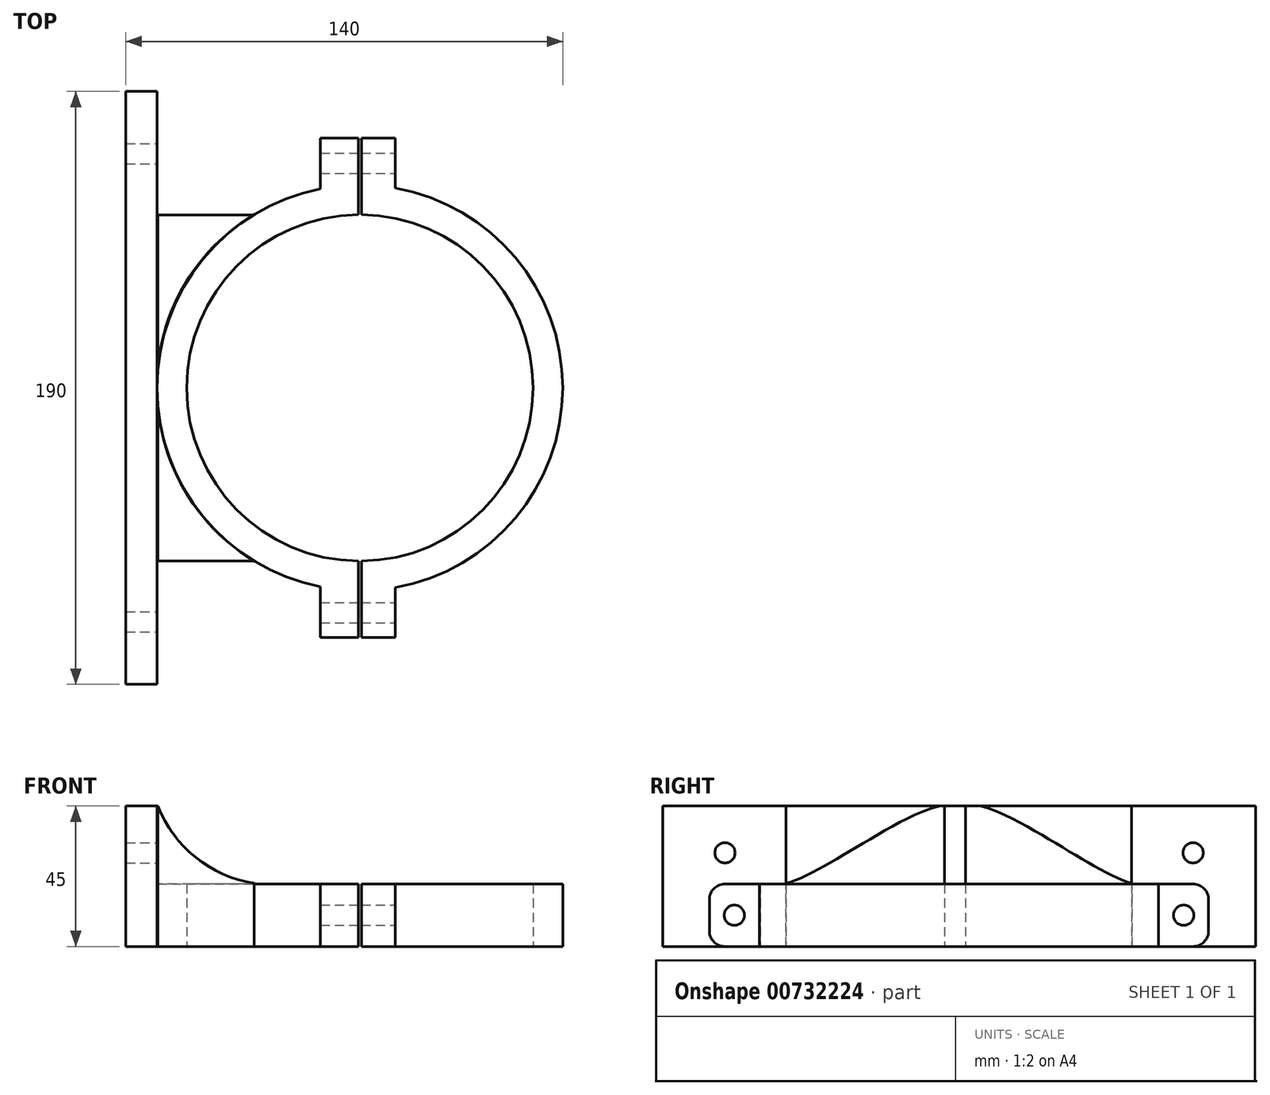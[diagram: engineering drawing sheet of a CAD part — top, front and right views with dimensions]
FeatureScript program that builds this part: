
annotation { "Feature Type Name" : "Feature", "Feature Type Description" : "" }
export const myFeature = defineFeature(function(context is Context, id is Id, definition is map)
    precondition{}
    {
        {
            var Q0;
            Q0=qCreatedBy(makeId("Top.planeOp"),FACE);
            var sketch = newSketch(context, id + "F0", { "sketchPlane" : qUnion([Q0])});
            skCircle(sketch, "E0", {"center": v(0, 0) * mm, "radius": 55.5 * mm});
            skCircle(sketch, "E1", {"center": v(0, 0) * mm, "radius": 65 * mm});
            skLineSegment(sketch, "E2.bottom", {"start": v(-75, 95) * mm, "end": v(-65, 95) * mm});
            skLineSegment(sketch, "E2.top", {"start": v(-75, -95) * mm, "end": v(-65, -95) * mm});
            skLineSegment(sketch, "E2.left", {"start": v(-75, 95) * mm, "end": v(-75, -95) * mm});
            skLineSegment(sketch, "E2.right", {"start": v(-65, 95) * mm, "end": v(-65, -95) * mm});
            skLineSegment(sketch, "E3.bottom", {"start": v(-12.63, 80) * mm, "end": v(11.37, 80) * mm});
            skLineSegment(sketch, "E3.top", {"start": v(-12.63, -80) * mm, "end": v(11.37, -80) * mm});
            skLineSegment(sketch, "E3.left", {"start": v(-12.63, 80) * mm, "end": v(-12.63, 63.76) * mm});
            skLineSegment(sketch, "E3.right", {"start": v(11.37, 80) * mm, "end": v(11.37, 64) * mm});
            skLineSegment(sketch, "E4.trimOffspring", {"start": v(11.37, -64) * mm, "end": v(11.37, -80) * mm});
            skLineSegment(sketch, "E5.trimOffspring", {"start": v(-12.63, -63.76) * mm, "end": v(-12.63, -80) * mm});
            skSolve(sketch);
        }
        {
            var Q0;
            {var subQ1=sQuery(id+"F0.wireOp",EDGE,"E2.bottom");Q0=makeQuery(id+"F0.imprint","IMPRINT",FACE,{"disambiguationData":[TD([[makeQuery(id+"F0.imprint","IMPRINT",EDGE,{"derivedFrom":subQ1}),-1.0]])]});}
            var Q1;
            Q1=makeQuery(id+"F0.imprint","IMPRINT",FACE,{"disambiguationData":[TD([[makeQuery(id+"F0.imprint","IMPRINT",EDGE,{"derivedFrom":sQuery(id+"F0.wireOp",EDGE,"E0")}),-1.0]])]});
            var Q2;
            Q2=makeQuery(id+"F0.imprint","IMPRINT",FACE,{"disambiguationData":[TD([[makeQuery(id+"F0.imprint","IMPRINT",EDGE,{"derivedFrom":sQuery(id+"F0.wireOp",EDGE,"E3.bottom")}),-1.0]])]});
            var Q3;
            Q3=makeQuery(id+"F0.imprint","IMPRINT",FACE,{"disambiguationData":[TD([[makeQuery(id+"F0.imprint","IMPRINT",EDGE,{"derivedFrom":sQuery(id+"F0.wireOp",EDGE,"E3.top")}),1.0]])]});
            extrude(context, id + "F1", {"entities" : qUnion([Q0, Q1, Q2, Q3]), "depth" : 20 * mm, "offsetDistance" : 25 * mm});
        }
        {
            var Q0;
            Q0=makeQuery(id+"F1.opExtrude","SWEPT_FACE",FACE,{"disambiguationData":[OSD([sQuery(id+"F0.wireOp",EDGE,"E4.trimOffspring")])]});
            var sketch = newSketch(context, id + "F2", { "sketchPlane" : qUnion([Q0])});
            skCircle(sketch, "E6", {"center": v(-72, 10) * mm, "radius": 3.25 * mm});
            skPoint(sketch, "E6.centerSnap0", {"position": v(-80, 10) * mm});
            skCircle(sketch, "E7", {"center": v(72, 10) * mm, "radius": 3.25 * mm});
            skSolve(sketch);
        }
        {
            var Q0;
            Q0=makeQuery(id+"F2.imprint","IMPRINT",FACE,{"disambiguationData":[TD([[makeQuery(id+"F2.imprint","IMPRINT",EDGE,{"derivedFrom":sQuery(id+"F2.wireOp",EDGE,"E6")}),1.0]])]});
            var Q1;
            Q1=makeQuery(id+"F2.imprint","IMPRINT",FACE,{"disambiguationData":[TD([[makeQuery(id+"F2.imprint","IMPRINT",EDGE,{"derivedFrom":sQuery(id+"F2.wireOp",EDGE,"E7")}),1.0]])]});
            extrude(context, id + "F3", {"entities" : qUnion([Q0, Q1]), "operationType" : NewBodyOperationType.REMOVE, "endBound" : BoundingType.UP_TO_NEXT, "oppositeDirection" : true, "depth" : 25 * mm, "offsetDistance" : 25 * mm});
        }
        {
            var Q0;
            Q0=makeQuery(id+"F1.opExtrude","CAP_FACE",FACE,{"disambiguationData":[OSD([sQuery(id+"F0.wireOp",EDGE,"E2.bottom"),sQuery(id+"F0.wireOp",EDGE,"E2.top"),sQuery(id+"F0.wireOp",EDGE,"E2.left"),sQuery(id+"F0.wireOp",EDGE,"E2.right")])],"isStart":false});
            var sketch = newSketch(context, id + "F4", { "sketchPlane" : qUnion([Q0])});
            skLineSegment(sketch, "E8.bottom", {"start": v(-75, 95) * mm, "end": v(-65, 95) * mm});
            skLineSegment(sketch, "E8.top", {"start": v(-75, -95) * mm, "end": v(-65, -95) * mm});
            skLineSegment(sketch, "E8.left", {"start": v(-75, 95) * mm, "end": v(-75, -95) * mm});
            skLineSegment(sketch, "E8.right", {"start": v(-65, 95) * mm, "end": v(-65, -95) * mm});
            skSolve(sketch);
        }
        {
            var Q0;
            Q0=makeQuery(id+"F4.imprint","IMPRINT",FACE,{"disambiguationData":[TD([[makeQuery(id+"F4.imprint","IMPRINT",EDGE,{"derivedFrom":sQuery(id+"F4.wireOp",EDGE,"E8.bottom")}),-1.0]])]});
            extrude(context, id + "F5", {"entities" : qUnion([Q0]), "operationType" : NewBodyOperationType.ADD, "depth" : 25 * mm, "offsetDistance" : 25 * mm});
        }
        {
            var Q0;
            Q0=makeQuery(id+"F1.opExtrude","CAP_FACE",FACE,{"disambiguationData":[OSD([sQuery(id+"F0.wireOp",EDGE,"E0"),sQuery(id+"F0.wireOp",EDGE,"E1"),sQuery(id+"F0.wireOp",EDGE,"E3.bottom"),sQuery(id+"F0.wireOp",EDGE,"E3.top"),sQuery(id+"F0.wireOp",EDGE,"E3.left"),sQuery(id+"F0.wireOp",EDGE,"E3.right"),sQuery(id+"F0.wireOp",EDGE,"E4.trimOffspring"),sQuery(id+"F0.wireOp",EDGE,"E5.trimOffspring")])],"isStart":true});
            var sketch = newSketch(context, id + "F6", { "sketchPlane" : qUnion([Q0])});
            skLineSegment(sketch, "E9", {"start": v(-33.92, 55.45) * mm, "end": v(-64.72, 55.45) * mm});
            skLineSegment(sketch, "E10", {"start": v(-34.05, -55.37) * mm, "end": v(-64.72, -55.37) * mm});
            skArc(sketch, "E11", {"start": v(-33.92, 55.45) * mm, "mid": v(-55.58, 33.8) * mm, "end": v(-64.84, 4.62) * mm});
            skArc(sketch, "E12", {"start": v(-65, 0) * mm, "mid": v(-56.9, -31.8) * mm, "end": v(-34.05, -55.37) * mm});
            skLineSegment(sketch, "E13", {"start": v(-64.72, 55.45) * mm, "end": v(-64.84, 4.62) * mm});
            skLineSegment(sketch, "E14", {"start": v(-65, 0) * mm, "end": v(-64.72, -55.37) * mm});
            skSolve(sketch);
        }
        {
            var Q0;
            Q0=makeQuery(id+"F6.imprint","IMPRINT",FACE,{"disambiguationData":[TD([[makeQuery(id+"F6.imprint","IMPRINT",EDGE,{"derivedFrom":sQuery(id+"F6.wireOp",EDGE,"E9")}),1.0]])]});
            var Q1;
            {var subQ0=sQuery(id+"F6.wireOp",EDGE,"E10");Q1=makeQuery(id+"F6.imprint","IMPRINT",FACE,{"disambiguationData":[TD([[makeQuery(id+"F6.imprint","IMPRINT",EDGE,{"derivedFrom":subQ0}),-1.0]])]});}
            extrude(context, id + "F7", {"entities" : qUnion([Q0, Q1]), "oppositeDirection" : true, "depth" : 45 * mm, "offsetDistance" : 25 * mm});
        }
        {
            var Q0;
            Q0=makeQuery(id+"F7.opExtrude","SWEPT_FACE",FACE,{"disambiguationData":[OSD([sQuery(id+"F6.wireOp",EDGE,"E9")])]});
            var sketch = newSketch(context, id + "F8", { "sketchPlane" : qUnion([Q0])});
            skArc(sketch, "E15", {"start": v(-64.72, 45) * mm, "mid": v(-52.58, 28.55) * mm, "end": v(-33.92, 20.21) * mm});
            skLineSegment(sketch, "E16", {"start": v(-64.72, 45) * mm, "end": v(-33.92, 45) * mm});
            skLineSegment(sketch, "E17", {"start": v(-33.92, 45) * mm, "end": v(-33.92, 20.21) * mm});
            skSolve(sketch);
        }
        {
            var Q0;
            Q0=makeQuery(id+"F8.imprint","IMPRINT",FACE,{"disambiguationData":[TD([[makeQuery(id+"F8.imprint","IMPRINT",EDGE,{"derivedFrom":sQuery(id+"F8.wireOp",EDGE,"E15")}),1.0]])]});
            extrude(context, id + "F9", {"entities" : qUnion([Q0]), "operationType" : NewBodyOperationType.REMOVE, "oppositeDirection" : true, "depth" : 150 * mm, "offsetDistance" : 25 * mm});
        }
        {
            var Q0;
            Q0=makeQuery(id+"F5.boolean.opBoolean","MERGE",FACE,{"derivedFrom":[makeQuery(id+"F1.opExtrude","SWEPT_FACE",FACE,{"disambiguationData":[OSD([sQuery(id+"F0.wireOp",EDGE,"E2.right")])]}),makeQuery(id+"F5.opExtrude","SWEPT_FACE",FACE,{"disambiguationData":[OSD([sQuery(id+"F4.wireOp",EDGE,"E8.right")])]})]});
            var sketch = newSketch(context, id + "F10", { "sketchPlane" : qUnion([Q0])});
            skCircle(sketch, "E18", {"center": v(-75, 30) * mm, "radius": 3.25 * mm});
            skCircle(sketch, "E19", {"center": v(75, 30) * mm, "radius": 3.25 * mm});
            skSolve(sketch);
        }
        {
            var Q0;
            Q0=makeQuery(id+"F10.imprint","IMPRINT",FACE,{"disambiguationData":[TD([[makeQuery(id+"F10.imprint","IMPRINT",EDGE,{"derivedFrom":sQuery(id+"F10.wireOp",EDGE,"E18")}),1.0]])]});
            var Q1;
            Q1=makeQuery(id+"F10.imprint","IMPRINT",FACE,{"disambiguationData":[TD([[makeQuery(id+"F10.imprint","IMPRINT",EDGE,{"derivedFrom":sQuery(id+"F10.wireOp",EDGE,"E19")}),1.0]])]});
            extrude(context, id + "F11", {"entities" : qUnion([Q0, Q1]), "operationType" : NewBodyOperationType.REMOVE, "oppositeDirection" : true, "depth" : 25 * mm, "offsetDistance" : 25 * mm});
        }
        {
            var Q0;
            Q0=makeQuery(id+"F1.opExtrude","CAP_FACE",FACE,{"disambiguationData":[OSD([sQuery(id+"F0.wireOp",EDGE,"E0"),sQuery(id+"F0.wireOp",EDGE,"E1"),sQuery(id+"F0.wireOp",EDGE,"E3.bottom"),sQuery(id+"F0.wireOp",EDGE,"E3.top"),sQuery(id+"F0.wireOp",EDGE,"E3.left"),sQuery(id+"F0.wireOp",EDGE,"E3.right"),sQuery(id+"F0.wireOp",EDGE,"E4.trimOffspring"),sQuery(id+"F0.wireOp",EDGE,"E5.trimOffspring")])],"isStart":false});
            var sketch = newSketch(context, id + "F12", { "sketchPlane" : qUnion([Q0])});
            skLineSegment(sketch, "E20.bottom", {"start": v(-0.5, 86.3) * mm, "end": v(0.5, 86.3) * mm});
            skLineSegment(sketch, "E20.top", {"start": v(-0.5, -88.7) * mm, "end": v(0.5, -88.7) * mm});
            skLineSegment(sketch, "E20.left", {"start": v(-0.5, 86.3) * mm, "end": v(-0.5, -88.7) * mm});
            skLineSegment(sketch, "E20.right", {"start": v(0.5, 86.3) * mm, "end": v(0.5, -88.7) * mm});
            skSolve(sketch);
        }
        {
            var Q0;
            {var subQ0=sQuery(id+"F12.wireOp",EDGE,"E20.left");var subQ1=makeQuery(id+"F1.opExtrude","CAP_EDGE",EDGE,{"disambiguationData":[OSD([sQuery(id+"F0.wireOp",EDGE,"E3.bottom")])],"isStart":false});var subQ2=makeQuery(id+"F12.imprint","INTERSECT",VERTEX,{"derivedFrom":[subQ1,subQ0]});Q0=makeQuery(id+"F12.imprint","IMPRINT",FACE,{"disambiguationData":[TD([[makeQuery(id+"F12.imprint","IMPRINT",EDGE,{"disambiguationData":[TD([[subQ2,-1.0]])],"derivedFrom":subQ0}),1.0]])]});}
            var Q1;
            {var subQ0=sQuery(id+"F12.wireOp",EDGE,"E20.left");var subQ1=makeQuery(id+"F1.opExtrude","CAP_EDGE",EDGE,{"disambiguationData":[OSD([sQuery(id+"F0.wireOp",EDGE,"E3.top")])],"isStart":false});var subQ2=makeQuery(id+"F12.imprint","INTERSECT",VERTEX,{"derivedFrom":[subQ1,subQ0]});Q1=makeQuery(id+"F12.imprint","IMPRINT",FACE,{"disambiguationData":[TD([[makeQuery(id+"F12.imprint","IMPRINT",EDGE,{"disambiguationData":[TD([[subQ2,1.0]])],"derivedFrom":subQ0}),1.0]])]});}
            extrude(context, id + "F13", {"entities" : qUnion([Q0, Q1]), "operationType" : NewBodyOperationType.REMOVE, "oppositeDirection" : true, "depth" : 25 * mm, "offsetDistance" : 25 * mm});
        }
        {
            var Q0;
            {var subQ0=sQuery(id+"F0.wireOp",EDGE,"E5.trimOffspring");var subQ1=sQuery(id+"F0.wireOp",EDGE,"E3.top");Q0=makeQuery(id+"F13.boolean.opBoolean","SPLIT",EDGE,{"disambiguationData":[TD([makeQuery(id+"F1.opExtrude","SWEPT_FACE",FACE,{"disambiguationData":[OSD([subQ0])]})])],"derivedFrom":makeQuery(id+"F1.opExtrude","CAP_EDGE",EDGE,{"disambiguationData":[OSD([subQ1])],"isStart":true})});}
            var Q1;
            {var subQ0=sQuery(id+"F0.wireOp",EDGE,"E4.trimOffspring");var subQ1=sQuery(id+"F0.wireOp",EDGE,"E3.top");Q1=makeQuery(id+"F13.boolean.opBoolean","SPLIT",EDGE,{"disambiguationData":[TD([makeQuery(id+"F1.opExtrude","SWEPT_FACE",FACE,{"disambiguationData":[OSD([subQ0])]})])],"derivedFrom":makeQuery(id+"F1.opExtrude","CAP_EDGE",EDGE,{"disambiguationData":[OSD([subQ1])],"isStart":true})});}
            var Q2;
            {var subQ0=sQuery(id+"F0.wireOp",EDGE,"E4.trimOffspring");var subQ1=sQuery(id+"F0.wireOp",EDGE,"E3.top");var subQ4=makeQuery(id+"F1.opExtrude","CAP_EDGE",EDGE,{"disambiguationData":[OSD([subQ1])],"isStart":false});Q2=makeQuery(id+"F13.boolean.opBoolean","SPLIT",EDGE,{"disambiguationData":[TD([makeQuery(id+"F1.opExtrude","SWEPT_FACE",FACE,{"disambiguationData":[OSD([subQ0])]})])],"derivedFrom":subQ4});}
            var Q3;
            {var subQ0=sQuery(id+"F0.wireOp",EDGE,"E5.trimOffspring");var subQ1=sQuery(id+"F0.wireOp",EDGE,"E3.top");var subQ4=makeQuery(id+"F1.opExtrude","CAP_EDGE",EDGE,{"disambiguationData":[OSD([subQ1])],"isStart":false});Q3=makeQuery(id+"F13.boolean.opBoolean","SPLIT",EDGE,{"disambiguationData":[TD([makeQuery(id+"F1.opExtrude","SWEPT_FACE",FACE,{"disambiguationData":[OSD([subQ0])]})])],"derivedFrom":subQ4});}
            var Q4;
            {var subQ0=sQuery(id+"F0.wireOp",EDGE,"E3.left");var subQ1=sQuery(id+"F0.wireOp",EDGE,"E3.bottom");Q4=makeQuery(id+"F13.boolean.opBoolean","SPLIT",EDGE,{"disambiguationData":[TD([makeQuery(id+"F1.opExtrude","SWEPT_FACE",FACE,{"disambiguationData":[OSD([subQ0])]})])],"derivedFrom":makeQuery(id+"F1.opExtrude","CAP_EDGE",EDGE,{"disambiguationData":[OSD([subQ1])],"isStart":true})});}
            var Q5;
            {var subQ0=sQuery(id+"F0.wireOp",EDGE,"E3.right");var subQ1=sQuery(id+"F0.wireOp",EDGE,"E3.bottom");Q5=makeQuery(id+"F13.boolean.opBoolean","SPLIT",EDGE,{"disambiguationData":[TD([makeQuery(id+"F1.opExtrude","SWEPT_FACE",FACE,{"disambiguationData":[OSD([subQ0])]})])],"derivedFrom":makeQuery(id+"F1.opExtrude","CAP_EDGE",EDGE,{"disambiguationData":[OSD([subQ1])],"isStart":true})});}
            var Q6;
            {var subQ0=sQuery(id+"F0.wireOp",EDGE,"E3.left");var subQ1=sQuery(id+"F0.wireOp",EDGE,"E3.bottom");var subQ4=makeQuery(id+"F1.opExtrude","CAP_EDGE",EDGE,{"disambiguationData":[OSD([subQ1])],"isStart":false});Q6=makeQuery(id+"F13.boolean.opBoolean","SPLIT",EDGE,{"disambiguationData":[TD([makeQuery(id+"F1.opExtrude","SWEPT_FACE",FACE,{"disambiguationData":[OSD([subQ0])]})])],"derivedFrom":subQ4});}
            var Q7;
            {var subQ0=sQuery(id+"F0.wireOp",EDGE,"E3.right");var subQ1=sQuery(id+"F0.wireOp",EDGE,"E3.bottom");var subQ4=makeQuery(id+"F1.opExtrude","CAP_EDGE",EDGE,{"disambiguationData":[OSD([subQ1])],"isStart":false});Q7=makeQuery(id+"F13.boolean.opBoolean","SPLIT",EDGE,{"disambiguationData":[TD([makeQuery(id+"F1.opExtrude","SWEPT_FACE",FACE,{"disambiguationData":[OSD([subQ0])]})])],"derivedFrom":subQ4});}
            fillet(context, id + "F14", {"entities" : qUnion([Q0, Q1, Q2, Q3, Q4, Q5, Q6, Q7]), "radius" : 5 * mm, "tangentPropagation" : true, "allowEdgeOverflow" : false});
        }
    });
